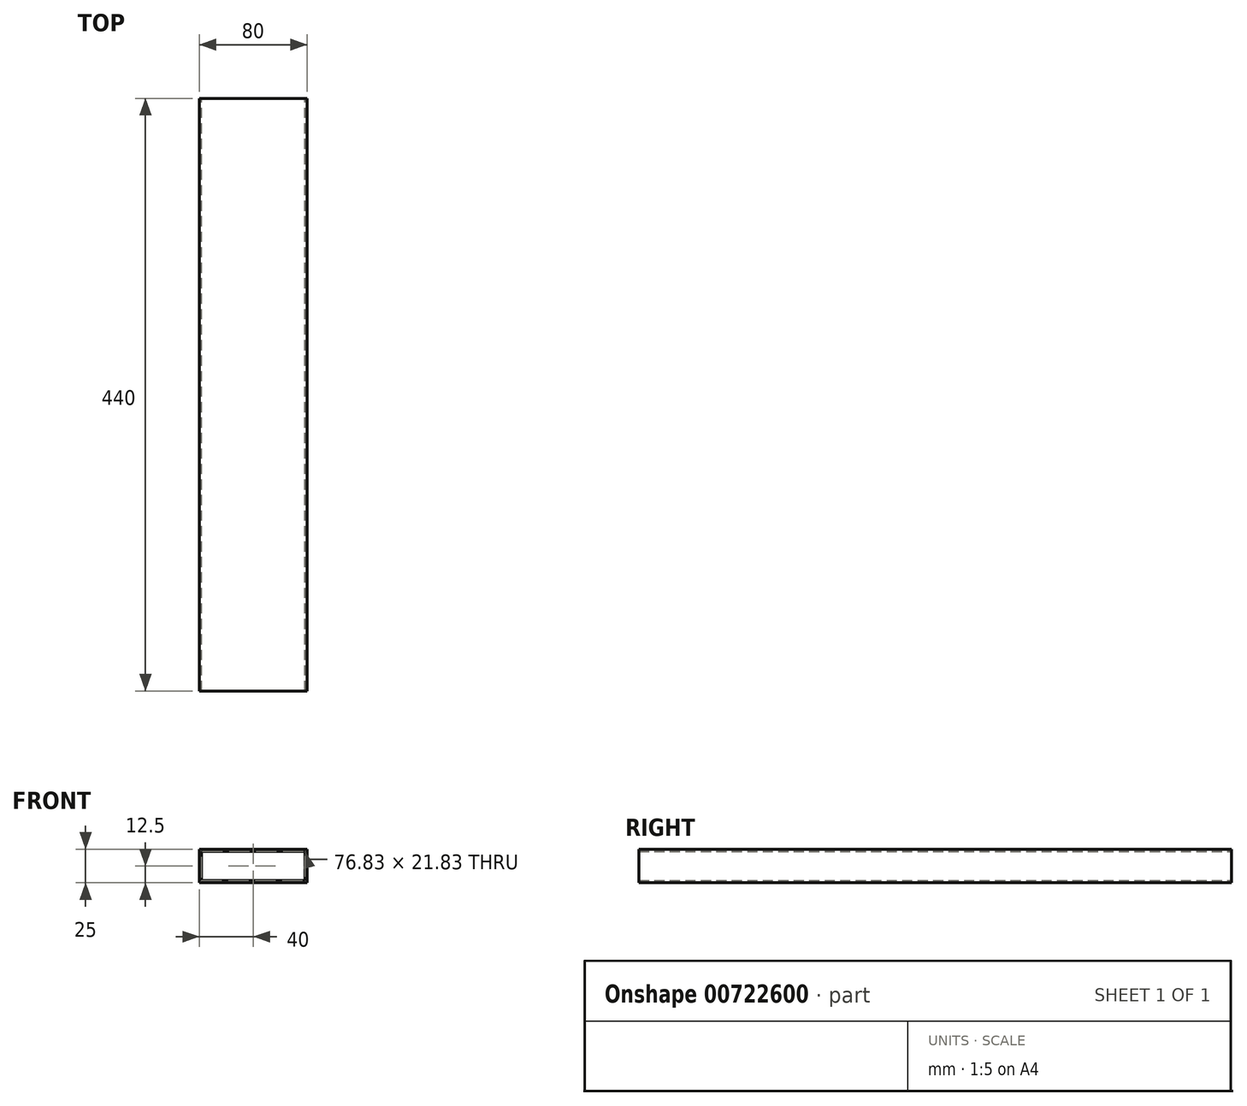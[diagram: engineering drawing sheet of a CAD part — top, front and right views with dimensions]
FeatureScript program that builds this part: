
annotation { "Feature Type Name" : "Feature", "Feature Type Description" : "" }
export const myFeature = defineFeature(function(context is Context, id is Id, definition is map)
    precondition{}
    {
        {
            var Q0;
            Q0=qCreatedBy(makeId("Front.planeOp"),FACE);
            var sketch = newSketch(context, id + "F0", { "sketchPlane" : qUnion([Q0])});
            skLineSegment(sketch, "E0.bottom", {"start": v(-40, -12.5) * mm, "end": v(40, -12.5) * mm});
            skLineSegment(sketch, "E0.top", {"start": v(-40, 12.5) * mm, "end": v(40, 12.5) * mm});
            skLineSegment(sketch, "E0.left", {"start": v(-40, -12.5) * mm, "end": v(-40, 12.5) * mm});
            skLineSegment(sketch, "E0.right", {"start": v(40, -12.5) * mm, "end": v(40, 12.5) * mm});
            skPoint(sketch, "E0.middle", {"position": v(0, 0) * mm});
            skLineSegment(sketch, "E1.bottom", {"start": v(-38.41, -10.91) * mm, "end": v(38.41, -10.91) * mm});
            skLineSegment(sketch, "E1.top", {"start": v(-38.41, 10.91) * mm, "end": v(38.41, 10.91) * mm});
            skLineSegment(sketch, "E1.left", {"start": v(-38.41, -10.91) * mm, "end": v(-38.41, 10.91) * mm});
            skLineSegment(sketch, "E1.right", {"start": v(38.41, -10.91) * mm, "end": v(38.41, 10.91) * mm});
            skSolve(sketch);
        }
        {
            var Q0;
            Q0=makeQuery(id+"F0.imprint","IMPRINT",FACE,{"disambiguationData":[TD([[makeQuery(id+"F0.imprint","IMPRINT",EDGE,{"derivedFrom":sQuery(id+"F0.wireOp",EDGE,"E0.bottom")}),1.0]])]});
            extrude(context, id + "F1", {"entities" : qUnion([Q0]), "endBound" : BoundingType.SYMMETRIC, "depth" : 440 * mm, "offsetDistance" : 25 * mm});
        }
    });
